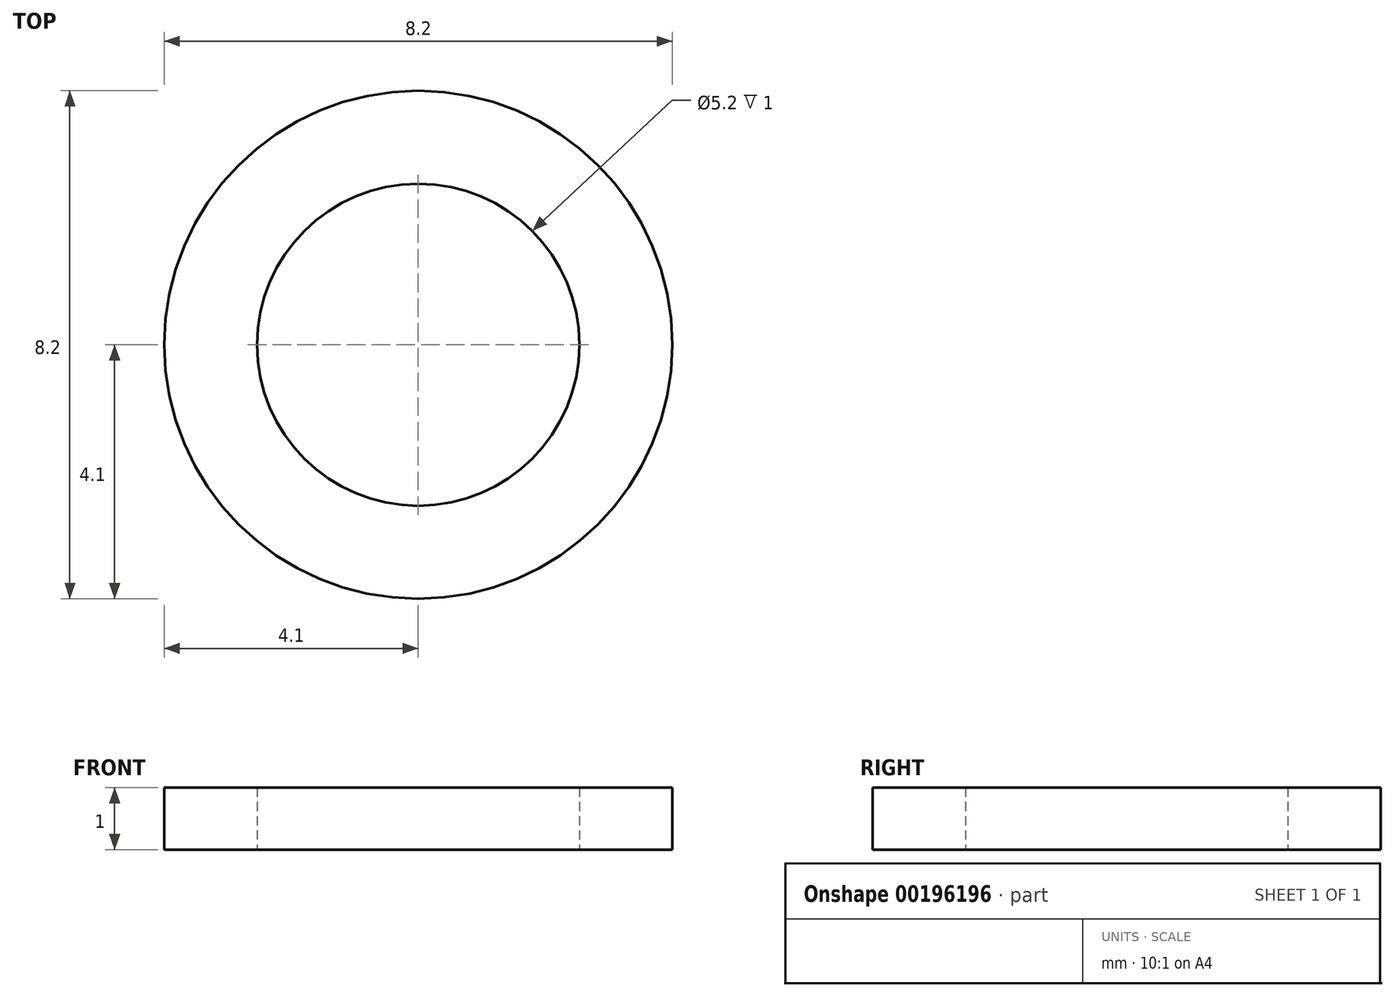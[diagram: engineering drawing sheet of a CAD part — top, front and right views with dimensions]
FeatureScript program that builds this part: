
annotation { "Feature Type Name" : "Feature", "Feature Type Description" : "" }
export const myFeature = defineFeature(function(context is Context, id is Id, definition is map)
    precondition{}
    {
        {
            var Q0;
            Q0=qCreatedBy(makeId("Top.planeOp"),FACE);
            var sketch = newSketch(context, id + "F0", { "sketchPlane" : qUnion([Q0])});
            skCircle(sketch, "E0", {"center": v(0, 0) * mm, "radius": 2.6 * mm});
            skCircle(sketch, "E1.0", {"center": v(0, 0) * mm, "radius": 4.1 * mm});
            skSolve(sketch);
        }
        {
            var Q0;
            Q0=makeQuery(id+"F0.imprint","IMPRINT",FACE,{"disambiguationData":[TD([[makeQuery(id+"F0.imprint","IMPRINT",EDGE,{"derivedFrom":sQuery(id+"F0.wireOp",EDGE,"E0")}),-1.0]])]});
            extrude(context, id + "F1", {"entities" : qUnion([Q0]), "depth" : 1 * mm});
        }
    });
